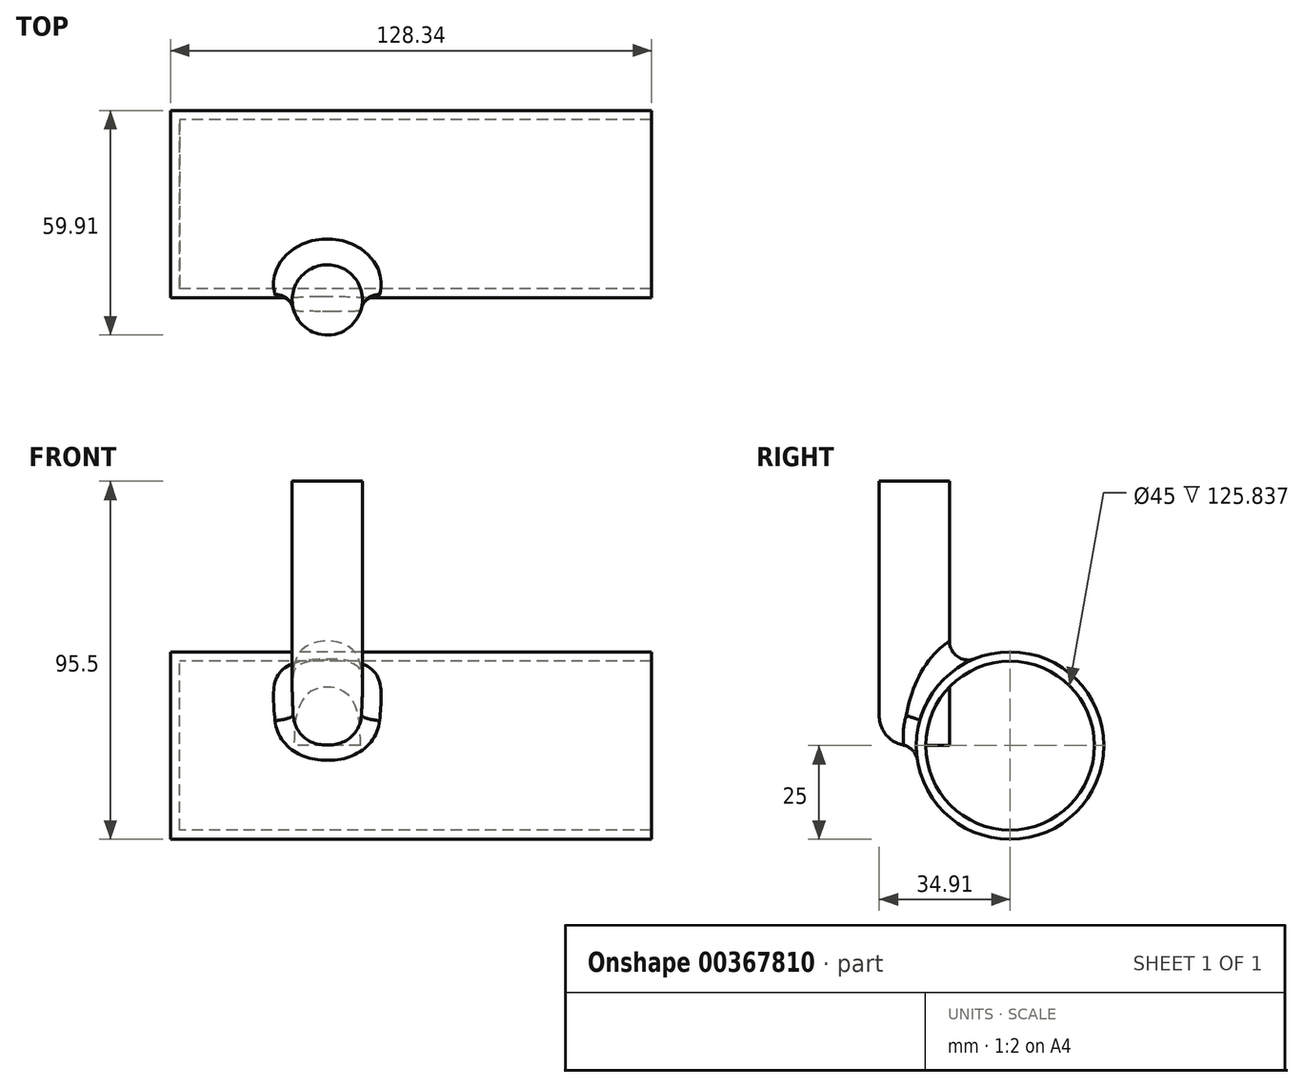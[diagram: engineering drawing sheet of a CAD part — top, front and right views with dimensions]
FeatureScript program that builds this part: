
annotation { "Feature Type Name" : "Feature", "Feature Type Description" : "" }
export const myFeature = defineFeature(function(context is Context, id is Id, definition is map)
    precondition{}
    {
        {
            var Q0;
            Q0=qCreatedBy(makeId("Right.planeOp"),FACE);
            var sketch = newSketch(context, id + "F0", { "sketchPlane" : qUnion([Q0])});
            skCircle(sketch, "E0", {"center": v(0, 0) * mm, "radius": 25 * mm});
            skSolve(sketch);
        }
        {
            var Q0;
            Q0=makeQuery(id+"F0.imprint","IMPRINT",FACE,{"disambiguationData":[TD([[makeQuery(id+"F0.imprint","IMPRINT",EDGE,{"derivedFrom":sQuery(id+"F0.wireOp",EDGE,"E0")}),1.0]])]});
            extrude(context, id + "F1", {"entities" : qUnion([Q0]), "depth" : 128.34 * mm});
        }
        {
            var Q0;
            Q0=makeQuery(id+"F1.opExtrude","CAP_FACE",FACE,{"disambiguationData":[OSD([sQuery(id+"F0.wireOp",EDGE,"E0")])],"isStart":false});
            shell(context, id + "F2", {"entities" : qUnion([Q0]), "thickness" : 2.5 * mm});
        }
        {
            var Q0;
            Q0=qCreatedBy(makeId("Top.planeOp"),FACE);
            var sketch = newSketch(context, id + "F3", { "sketchPlane" : qUnion([Q0])});
            skCircle(sketch, "E1", {"center": v(41.86, -25.54) * mm, "radius": 9.37 * mm});
            skSolve(sketch);
        }
        {
            var Q0;
            Q0 = qSketchRegion(id + "F3", true);
            extrude(context, id + "F4", {"entities" : qUnion([Q0]), "operationType" : NewBodyOperationType.ADD, "depth" : 70.5 * mm});
        }
        {
            var Q0;
            {var subQ0=sQuery(id+"F3.wireOp",EDGE,"E1");Q0=makeQuery(id+"F4.boolean.opBoolean","SPLIT",EDGE,{"disambiguationData":[TD([makeQuery(id+"F1.opExtrude","SWEPT_FACE",FACE,{"disambiguationData":[OSD([sQuery(id+"F0.wireOp",EDGE,"E0")])]})])],"derivedFrom":makeQuery(id+"F4.opExtrude","CAP_EDGE",EDGE,{"disambiguationData":[OSD([subQ0])],"isStart":true})});}
            fillet(context, id + "F5", {"entities" : qUnion([Q0]), "radius" : 8 * mm, "tangentPropagation" : true, "allowEdgeOverflow" : false});
        }
        {
            var Q0;
            Q0=makeQuery(id+"F4.boolean.opBoolean","INTERSECT",EDGE,{"derivedFrom":[makeQuery(id+"F1.opExtrude","SWEPT_FACE",FACE,{"disambiguationData":[OSD([sQuery(id+"F0.wireOp",EDGE,"E0")])]}),makeQuery(id+"F4.opExtrude","SWEPT_FACE",FACE,{"disambiguationData":[OSD([sQuery(id+"F3.wireOp",EDGE,"E1")])]})]});
            fillet(context, id + "F6", {"entities" : qUnion([Q0]), "radius" : 5 * mm, "tangentPropagation" : true, "allowEdgeOverflow" : false});
        }
    });
